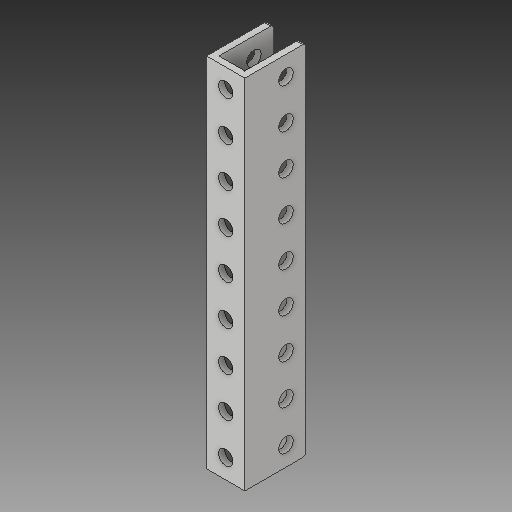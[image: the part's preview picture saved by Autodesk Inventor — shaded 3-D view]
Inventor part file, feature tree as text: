
AUTODESK INVENTOR PART (.ipt)
format: ipt  version: 2019 (Build 230136000, 136)  size: 140,800 bytes
history: native  units: in
note: dims shown in document units (in); Inventor stores cm internally (conversion verified against a paired STEP export)
features: fillet x1
ambient origin geometry x8: Origin, YZ Plane, XZ Plane, XY Plane, X Axis, Y Axis, Z Axis, Center Point
bodies: Solid1 (feature_tree)
feature tree (1):
  fillet  "Fillet1"  [1 undecoded]
note: 1 required parameter value undecoded (feature->parameter linkage not recoverable at this tier; creation-order binding heuristic only, values carry confidence <= 0.55)
